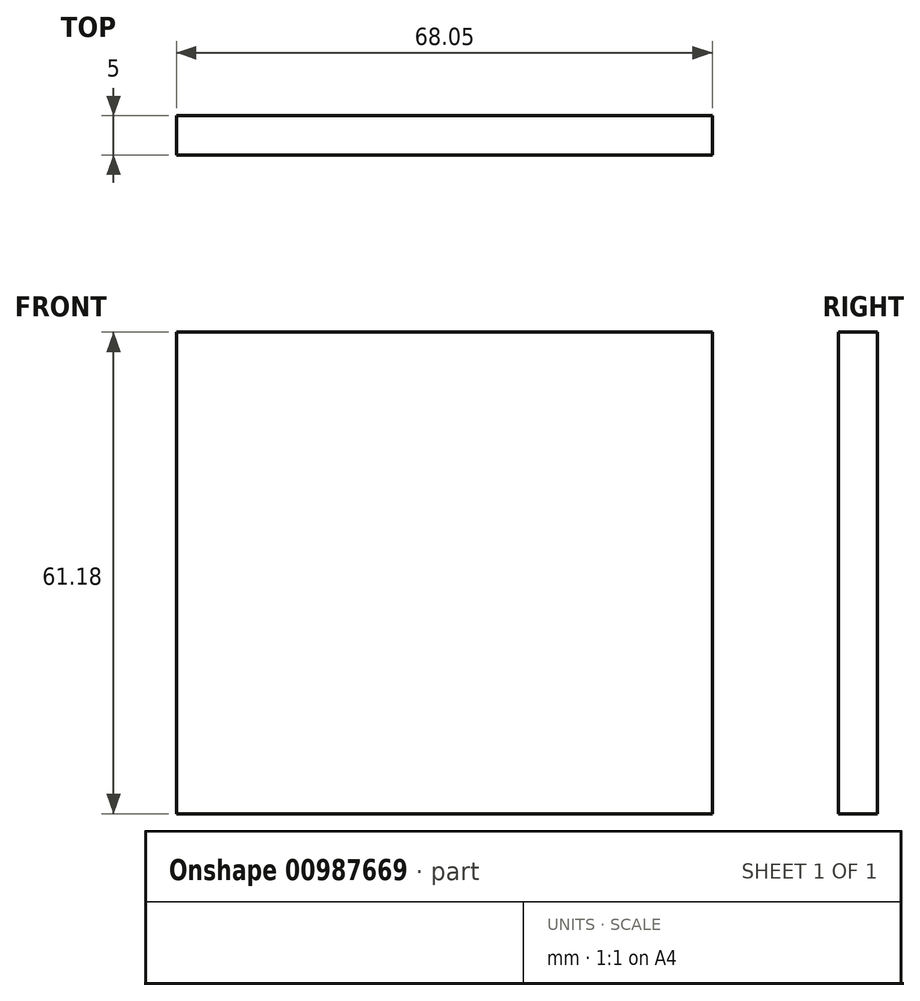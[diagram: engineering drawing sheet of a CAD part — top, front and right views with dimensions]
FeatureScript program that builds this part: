
annotation { "Feature Type Name" : "Feature", "Feature Type Description" : "" }
export const myFeature = defineFeature(function(context is Context, id is Id, definition is map)
    precondition{}
    {
        {
            var Q0;
            Q0=qCreatedBy(makeId("Front.planeOp"),FACE);
            var sketch = newSketch(context, id + "F0", { "sketchPlane" : qUnion([Q0])});
            skLineSegment(sketch, "E0.bottom", {"start": v(-17.83, 30.35) * mm, "end": v(50.22, 30.35) * mm});
            skLineSegment(sketch, "E0.top", {"start": v(-17.83, -30.83) * mm, "end": v(50.22, -30.83) * mm});
            skLineSegment(sketch, "E0.left", {"start": v(-17.83, 30.35) * mm, "end": v(-17.83, -30.83) * mm});
            skLineSegment(sketch, "E0.right", {"start": v(50.22, 30.35) * mm, "end": v(50.22, -30.83) * mm});
            skSolve(sketch);
        }
        {
            var Q0;
            Q0 = qSketchRegion(id + "F0", true);
            extrude(context, id + "F1", {"entities" : qUnion([Q0]), "depth" : 5 * mm, "offsetDistance" : 25 * mm});
        }
    });
